# Revit family: AD-P4T
name_source: partatom
category: Communication Devices
revit_build: Autodesk Revit 2014 (Build: 20130308_1515(x64)
units: mm (PartAtom-declared; Revit-internal decimal feet)

## types (1)
- AD-P4T
    100V Taps = 7.5, 15, 30
    70V Taps = 3.75, 7.5, 15, 30
    Coverage Horizontal = 150.00°
    Coverage Vertical = 150.00°
    Default Elevation = 0 mm
    Description = 4.5" 2-Way Pendant-Mount Loudspeaker

12-inch, Two-way Trapezoidal Enclosure with 90-degree Axisymmetric Coverage
    Impedance = 16
    Manufacturer = QSC Audio Products, LLC
    Manufacturer URL = qsc.com
    Model = AD-P4T
    Power Handling = 30
    Product Documentation Link = http://www.qsc.com
    Product Page URL = http://www.qsc.com
    Regulatory Compliance = UL1480, UL1876, RoHS, C-Tick, CE, UL94-V0, UL94-5VB
    SPL Max = 108
    Sensitivity = 87.9
    URL = http://www.qsc.com
    Weight Dimensional (kg) = 3.9
    Weight Dimensional (lb) = 8.7
    Weight Product (kg) = 2.9
    Weight Product (lb) = 6.5

## geometry (parser evidence)
native form markers: Blend x1, Sweep x1
no freeform markers — native parametric forms only
